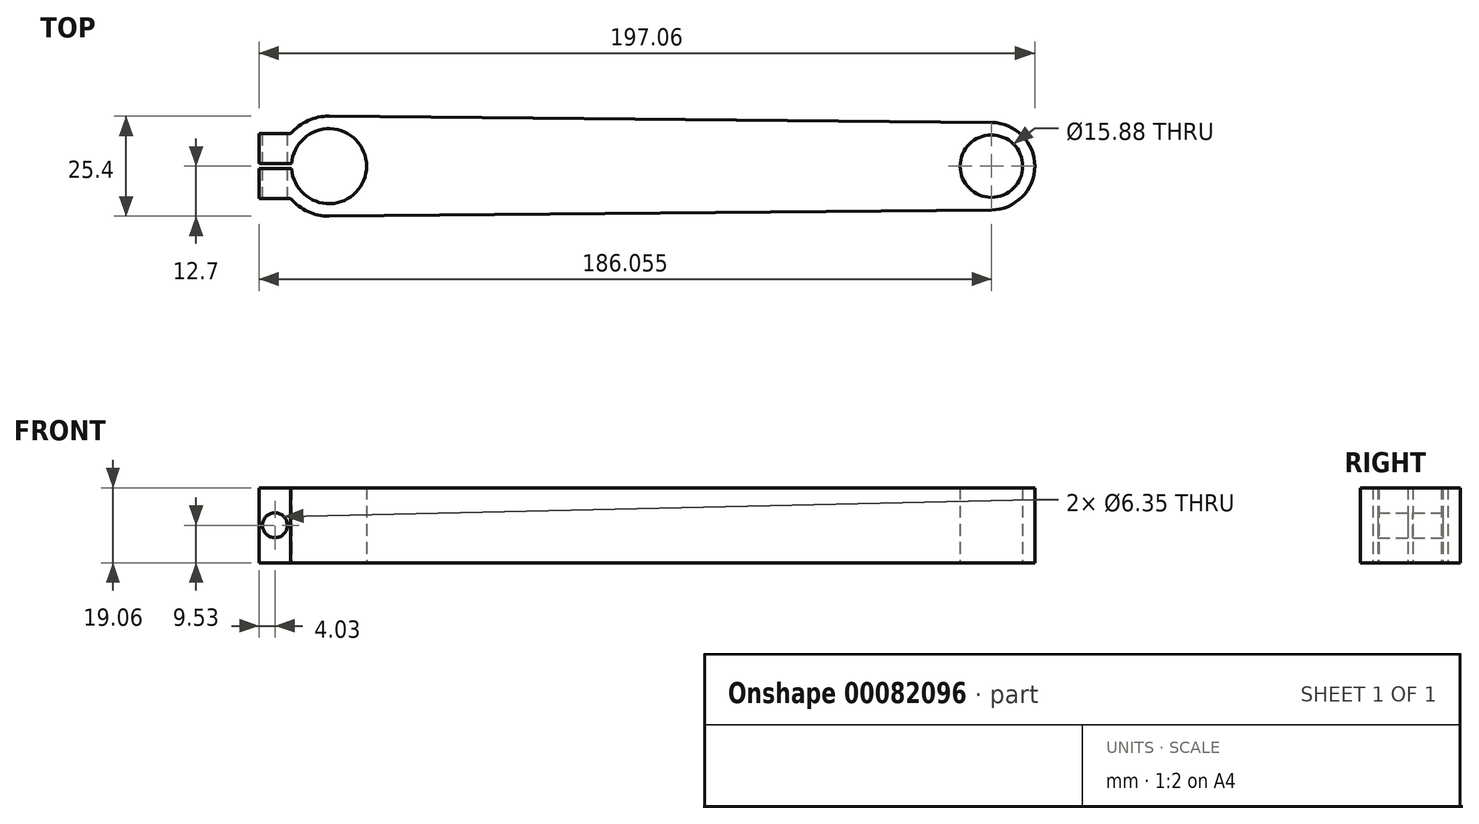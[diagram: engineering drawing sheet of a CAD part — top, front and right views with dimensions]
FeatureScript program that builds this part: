
annotation { "Feature Type Name" : "Feature", "Feature Type Description" : "" }
export const myFeature = defineFeature(function(context is Context, id is Id, definition is map)
    precondition{}
    {
        {
            var Q0;
            Q0=qCreatedBy(makeId("Top.planeOp"),FACE);
            var sketch = newSketch(context, id + "F0", { "sketchPlane" : qUnion([Q0])});
            skCircle(sketch, "E0.cCircle", {"center": v(0, 0) * mm, "radius": 7.79 * mm, "construction": true});
            skLineSegment(sketch, "E0.0", {"start": v(0.85, 8.95) * mm, "end": v(8.18, 3.75) * mm});
            skLineSegment(sketch, "E0.1", {"start": v(8.18, 3.75) * mm, "end": v(7.33, -5.2) * mm});
            skLineSegment(sketch, "E0.2", {"start": v(7.33, -5.2) * mm, "end": v(-0.85, -8.95) * mm});
            skLineSegment(sketch, "E0.3", {"start": v(-0.85, -8.95) * mm, "end": v(-8.18, -3.75) * mm});
            skLineSegment(sketch, "E0.4", {"start": v(-8.18, -3.75) * mm, "end": v(-7.33, 5.2) * mm});
            skLineSegment(sketch, "E0.5", {"start": v(-7.33, 5.2) * mm, "end": v(0.85, 8.95) * mm});
            skPoint(sketch, "E0.0.midPoint", {"position": v(4.51, 6.35) * mm});
            skPoint(sketch, "E1", {"position": v(0, 12.7) * mm});
            skPoint(sketch, "E2", {"position": v(0, -12.7) * mm});
            skCircle(sketch, "E3", {"center": v(0, 0) * mm, "radius": 9.53 * mm});
            skLineSegment(sketch, "E4", {"start": v(0, 12.7) * mm, "end": v(168.28, 11.11) * mm});
            skArc(sketch, "E5", {"start": v(168.28, -11.11) * mm, "mid": v(179.28, 0) * mm, "end": v(168.28, 11.11) * mm});
            skLineSegment(sketch, "E6", {"start": v(0, -12.7) * mm, "end": v(168.28, -11.11) * mm});
            skCircle(sketch, "E7", {"center": v(168.28, 0) * mm, "radius": 7.94 * mm});
            skLineSegment(sketch, "E8", {"start": v(-12.7, 0.64) * mm, "end": v(-9.5, 0.64) * mm});
            skLineSegment(sketch, "E9", {"start": v(-12.7, -0.64) * mm, "end": v(-9.5, -0.64) * mm});
            skLineSegment(sketch, "E10", {"start": v(-12.7, 0.64) * mm, "end": v(-17.78, 0.64) * mm});
            skLineSegment(sketch, "E11", {"start": v(-12.7, -0.64) * mm, "end": v(-17.78, -0.64) * mm});
            skLineSegment(sketch, "E12", {"start": v(-17.78, 0.64) * mm, "end": v(-17.78, 8.26) * mm});
            skLineSegment(sketch, "E13", {"start": v(-17.78, -0.64) * mm, "end": v(-17.78, -8.26) * mm});
            skLineSegment(sketch, "E14", {"start": v(-17.78, 8.26) * mm, "end": v(-9.72, 8.26) * mm});
            skLineSegment(sketch, "E15", {"start": v(-17.78, -8.26) * mm, "end": v(-9.72, -8.26) * mm});
            skArc(sketch, "E16", {"start": v(0, 12.7) * mm, "mid": v(-5.36, 11.56) * mm, "end": v(-9.72, 8.26) * mm});
            skArc(sketch, "E17", {"start": v(-9.72, -8.26) * mm, "mid": v(-5.36, -11.56) * mm, "end": v(0, -12.7) * mm});
            skSolve(sketch);
        }
        {
            var Q0;
            Q0=makeQuery(id+"F0.imprint","IMPRINT",FACE,{"disambiguationData":[TD([[makeQuery(id+"F0.imprint","IMPRINT",EDGE,{"derivedFrom":sQuery(id+"F0.wireOp",EDGE,"E4")}),-1.0]])]});
            extrude(context, id + "F1", {"entities" : qUnion([Q0]), "endBound" : BoundingType.SYMMETRIC, "depth" : 19.05 * mm});
        }
        {
            var Q0;
            Q0=makeQuery(id+"F1.opExtrude","SWEPT_FACE",FACE,{"disambiguationData":[OSD([sQuery(id+"F0.wireOp",EDGE,"E14")])]});
            var sketch = newSketch(context, id + "F2", { "sketchPlane" : qUnion([Q0])});
            skPoint(sketch, "E18", {"position": v(13.75, 0) * mm});
            skSolve(sketch);
        }
        {
            var Q0;
            Q0=sQuery(id+"F2.wireOp",VERTEX,"E18");
            var Q1;
            Q1=makeQuery(id+"F1.opExtrude","SWEPT_BODY",BODY,{"disambiguationData":[OSD([sQuery(id+"F0.wireOp",EDGE,"E3"),sQuery(id+"F0.wireOp",EDGE,"E4"),sQuery(id+"F0.wireOp",EDGE,"E5"),sQuery(id+"F0.wireOp",EDGE,"E6"),sQuery(id+"F0.wireOp",EDGE,"E7"),sQuery(id+"F0.wireOp",EDGE,"E8"),sQuery(id+"F0.wireOp",EDGE,"E9"),sQuery(id+"F0.wireOp",EDGE,"E10"),sQuery(id+"F0.wireOp",EDGE,"E11"),sQuery(id+"F0.wireOp",EDGE,"E12"),sQuery(id+"F0.wireOp",EDGE,"E13"),sQuery(id+"F0.wireOp",EDGE,"E14"),sQuery(id+"F0.wireOp",EDGE,"E15"),sQuery(id+"F0.wireOp",EDGE,"E16"),sQuery(id+"F0.wireOp",EDGE,"E17")])]});
            hole(context, id + "F3", {"style" : HoleStyle.SIMPLE, "endStyle" : HoleEndStyle.THROUGH, "holeDiameter" : 6.35 * mm, "locations" : qUnion([Q0]), "scope" : qUnion([Q1]), "isTappedThrough" : true});
        }
    });
